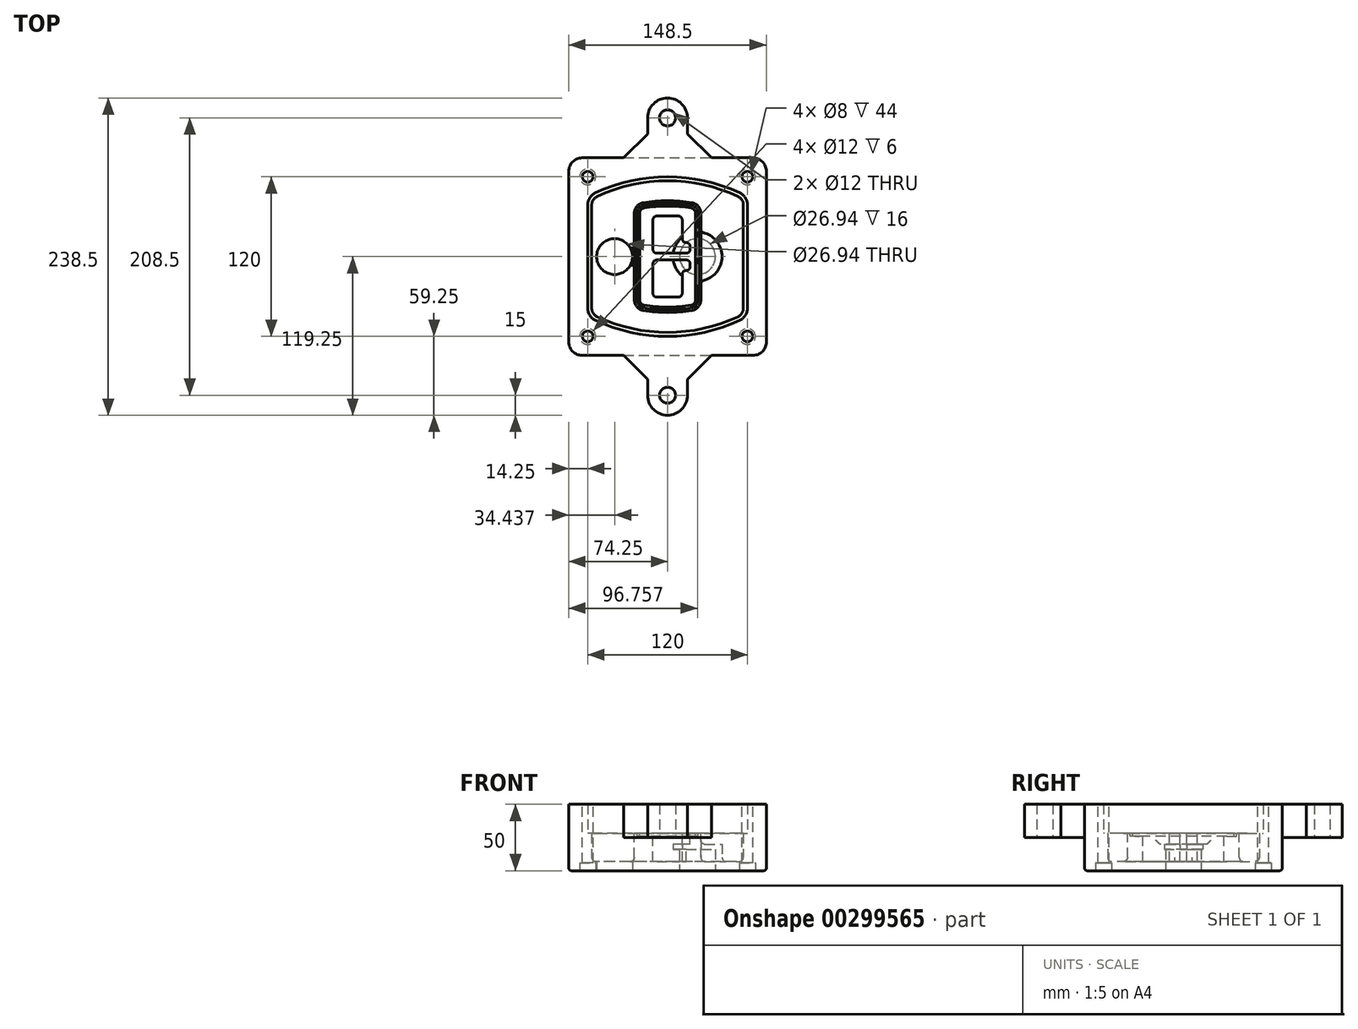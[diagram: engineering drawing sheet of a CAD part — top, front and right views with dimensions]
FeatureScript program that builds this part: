
annotation { "Feature Type Name" : "Feature", "Feature Type Description" : "" }
export const myFeature = defineFeature(function(context is Context, id is Id, definition is map)
    precondition{}
    {
        {
            var Q0;
            Q0=qCreatedBy(makeId("Top.planeOp"),FACE);
            var sketch = newSketch(context, id + "F0", { "sketchPlane" : qUnion([Q0])});
            skPoint(sketch, "E0.rect.middle", {"position": v(0, 0) * mm});
            skLineSegment(sketch, "E1.bottom", {"start": v(-64.25, -74.25) * mm, "end": v(64.25, -74.25) * mm});
            skLineSegment(sketch, "E1.top", {"start": v(-64.25, 74.25) * mm, "end": v(64.25, 74.25) * mm});
            skLineSegment(sketch, "E1.left", {"start": v(-74.25, -64.25) * mm, "end": v(-74.25, 64.25) * mm});
            skLineSegment(sketch, "E1.right", {"start": v(74.25, -64.25) * mm, "end": v(74.25, 64.25) * mm});
            skLineSegment(sketch, "E2", {"start": v(-74.25, 74.25) * mm, "end": v(74.25, -74.25) * mm, "construction": true});
            skLineSegment(sketch, "E3", {"start": v(74.25, 74.25) * mm, "end": v(-74.25, -74.25) * mm, "construction": true});
            skCircle(sketch, "E4", {"center": v(-60, 60) * mm, "radius": 4 * mm});
            skCircle(sketch, "E5", {"center": v(60, 60) * mm, "radius": 4 * mm});
            skCircle(sketch, "E6", {"center": v(60, -60) * mm, "radius": 4 * mm});
            skCircle(sketch, "E7", {"center": v(-60, -60) * mm, "radius": 4 * mm});
            skLineSegment(sketch, "E8", {"start": v(-60, 60) * mm, "end": v(60, 60) * mm, "construction": true});
            skLineSegment(sketch, "E9", {"start": v(60, 60) * mm, "end": v(60, -60) * mm, "construction": true});
            skLineSegment(sketch, "E10", {"start": v(60, -60) * mm, "end": v(-60, -60) * mm, "construction": true});
            skLineSegment(sketch, "E11", {"start": v(-60, -60) * mm, "end": v(-60, 60) * mm, "construction": true});
            skLineSegment(sketch, "E12", {"start": v(-60, 38.83) * mm, "end": v(-60, -38.83) * mm});
            skLineSegment(sketch, "E13", {"start": v(60, 38.83) * mm, "end": v(60, -38.83) * mm});
            skArc(sketch, "E14", {"start": v(54.26, 47.88) * mm, "mid": v(0, 60) * mm, "end": v(-54.26, 47.88) * mm});
            skArc(sketch, "E15", {"start": v(-54.26, -47.88) * mm, "mid": v(0, -60) * mm, "end": v(54.26, -47.88) * mm});
            skLineSegment(sketch, "E16", {"start": v(-60, 0) * mm, "end": v(60, 0) * mm, "construction": true});
            skPoint(sketch, "E17.visualSharp", {"position": v(-60, -45) * mm});
            skArc(sketch, "E17.filletArc", {"start": v(-60, -38.83) * mm, "mid": v(-58.44, -44.2) * mm, "end": v(-54.26, -47.88) * mm});
            skPoint(sketch, "E18.visualSharp", {"position": v(-60, 45) * mm});
            skArc(sketch, "E18.filletArc", {"start": v(-54.26, 47.88) * mm, "mid": v(-58.44, 44.2) * mm, "end": v(-60, 38.83) * mm});
            skPoint(sketch, "E19.visualSharp", {"position": v(60, 45) * mm});
            skArc(sketch, "E19.filletArc", {"start": v(60, 38.83) * mm, "mid": v(58.44, 44.2) * mm, "end": v(54.26, 47.88) * mm});
            skPoint(sketch, "E20.visualSharp", {"position": v(60, -45) * mm});
            skArc(sketch, "E20.filletArc", {"start": v(54.26, -47.88) * mm, "mid": v(58.44, -44.2) * mm, "end": v(60, -38.83) * mm});
            skPoint(sketch, "E21.visualSharp", {"position": v(-74.25, 74.25) * mm});
            skArc(sketch, "E21.filletArc", {"start": v(-64.25, 74.25) * mm, "mid": v(-71.32, 71.32) * mm, "end": v(-74.25, 64.25) * mm});
            skPoint(sketch, "E22.visualSharp", {"position": v(74.25, 74.25) * mm});
            skArc(sketch, "E22.filletArc", {"start": v(74.25, 64.25) * mm, "mid": v(71.32, 71.32) * mm, "end": v(64.25, 74.25) * mm});
            skPoint(sketch, "E23.visualSharp", {"position": v(74.25, -74.25) * mm});
            skArc(sketch, "E23.filletArc", {"start": v(64.25, -74.25) * mm, "mid": v(71.32, -71.32) * mm, "end": v(74.25, -64.25) * mm});
            skPoint(sketch, "E24.visualSharp", {"position": v(-74.25, -74.25) * mm});
            skArc(sketch, "E24.filletArc", {"start": v(-74.25, -64.25) * mm, "mid": v(-71.32, -71.32) * mm, "end": v(-64.25, -74.25) * mm});
            skArc(sketch, "E25.0", {"start": v(57, 38.83) * mm, "mid": v(55.9, 42.58) * mm, "end": v(52.98, 45.17) * mm});
            skLineSegment(sketch, "E25.1", {"start": v(57, 38.83) * mm, "end": v(57, -38.83) * mm});
            skArc(sketch, "E25.2", {"start": v(52.98, -45.17) * mm, "mid": v(55.9, -42.58) * mm, "end": v(57, -38.83) * mm});
            skArc(sketch, "E25.3", {"start": v(-52.98, -45.17) * mm, "mid": v(0, -57) * mm, "end": v(52.98, -45.17) * mm});
            skArc(sketch, "E25.4", {"start": v(-57, -38.83) * mm, "mid": v(-55.9, -42.58) * mm, "end": v(-52.98, -45.17) * mm});
            skArc(sketch, "E25.5", {"start": v(52.98, 45.17) * mm, "mid": v(0, 57) * mm, "end": v(-52.98, 45.17) * mm});
            skLineSegment(sketch, "E25.6", {"start": v(-57, 38.83) * mm, "end": v(-57, -38.83) * mm});
            skArc(sketch, "E25.7", {"start": v(-52.98, 45.17) * mm, "mid": v(-55.9, 42.58) * mm, "end": v(-57, 38.83) * mm});
            skArc(sketch, "E26.0", {"start": v(-55.96, 51.5) * mm, "mid": v(-61.82, 46.33) * mm, "end": v(-64, 38.83) * mm});
            skArc(sketch, "E26.1", {"start": v(55.96, 51.5) * mm, "mid": v(0, 64) * mm, "end": v(-55.96, 51.5) * mm});
            skArc(sketch, "E26.2", {"start": v(64, 38.83) * mm, "mid": v(61.82, 46.33) * mm, "end": v(55.96, 51.5) * mm});
            skLineSegment(sketch, "E26.3", {"start": v(64, 38.83) * mm, "end": v(64, -38.83) * mm});
            skArc(sketch, "E26.4", {"start": v(55.96, -51.5) * mm, "mid": v(61.82, -46.33) * mm, "end": v(64, -38.83) * mm});
            skLineSegment(sketch, "E26.5", {"start": v(-64, 38.83) * mm, "end": v(-64, -38.83) * mm});
            skArc(sketch, "E26.6", {"start": v(-55.96, -51.5) * mm, "mid": v(0, -64) * mm, "end": v(55.96, -51.5) * mm});
            skArc(sketch, "E26.7", {"start": v(-64, -38.83) * mm, "mid": v(-61.82, -46.33) * mm, "end": v(-55.96, -51.5) * mm});
            skSolve(sketch);
        }
        {
            var Q0;
            Q0=makeQuery(id+"F0.imprint","IMPRINT",FACE,{"disambiguationData":[TD([[makeQuery(id+"F0.imprint","IMPRINT",EDGE,{"derivedFrom":sQuery(id+"F0.wireOp",EDGE,"E1.bottom")}),1.0]])]});
            var Q1;
            Q1=makeQuery(id+"F0.imprint","IMPRINT",FACE,{"disambiguationData":[TD([[makeQuery(id+"F0.imprint","IMPRINT",EDGE,{"derivedFrom":sQuery(id+"F0.wireOp",EDGE,"E12")}),1.0]])]});
            var Q2;
            Q2=makeQuery(id+"F0.imprint","IMPRINT",FACE,{"disambiguationData":[TD([[makeQuery(id+"F0.imprint","IMPRINT",EDGE,{"derivedFrom":sQuery(id+"F0.wireOp",EDGE,"E25.0")}),1.0]])]});
            var Q3;
            Q3=makeQuery(id+"F0.imprint","IMPRINT",FACE,{"disambiguationData":[TD([[makeQuery(id+"F0.imprint","IMPRINT",EDGE,{"derivedFrom":sQuery(id+"F0.wireOp",EDGE,"E12")}),-1.0]])]});
            extrude(context, id + "F1", {"entities" : qUnion([Q0, Q1, Q2, Q3]), "oppositeDirection" : true, "depth" : 25 * mm});
        }
        {
            var Q0;
            Q0=makeQuery(id+"F0.imprint","IMPRINT",FACE,{"disambiguationData":[TD([[makeQuery(id+"F0.imprint","IMPRINT",EDGE,{"derivedFrom":sQuery(id+"F0.wireOp",EDGE,"E12")}),1.0]])]});
            extrude(context, id + "F2", {"entities" : qUnion([Q0]), "operationType" : NewBodyOperationType.ADD, "depth" : 3 * mm});
        }
        {
            var Q0;
            Q0=makeQuery(id+"F0.imprint","IMPRINT",FACE,{"disambiguationData":[TD([[makeQuery(id+"F0.imprint","IMPRINT",EDGE,{"derivedFrom":sQuery(id+"F0.wireOp",EDGE,"E25.0")}),1.0]])]});
            extrude(context, id + "F3", {"entities" : qUnion([Q0]), "operationType" : NewBodyOperationType.REMOVE, "oppositeDirection" : true, "depth" : 18 * mm});
        }
        {
            var Q0;
            Q0=makeQuery(id+"F2.opExtrude","CAP_FACE",FACE,{"disambiguationData":[OSD([sQuery(id+"F0.wireOp",EDGE,"E12"),sQuery(id+"F0.wireOp",EDGE,"E13"),sQuery(id+"F0.wireOp",EDGE,"E14"),sQuery(id+"F0.wireOp",EDGE,"E15"),sQuery(id+"F0.wireOp",EDGE,"E17.filletArc"),sQuery(id+"F0.wireOp",EDGE,"E18.filletArc"),sQuery(id+"F0.wireOp",EDGE,"E19.filletArc"),sQuery(id+"F0.wireOp",EDGE,"E20.filletArc"),sQuery(id+"F0.wireOp",EDGE,"E25.0"),sQuery(id+"F0.wireOp",EDGE,"E25.1"),sQuery(id+"F0.wireOp",EDGE,"E25.2"),sQuery(id+"F0.wireOp",EDGE,"E25.3"),sQuery(id+"F0.wireOp",EDGE,"E25.4"),sQuery(id+"F0.wireOp",EDGE,"E25.5"),sQuery(id+"F0.wireOp",EDGE,"E25.6"),sQuery(id+"F0.wireOp",EDGE,"E25.7")])],"isStart":false});
            var sketch = newSketch(context, id + "F4", { "sketchPlane" : qUnion([Q0])});
            skArc(sketch, "E27.0", {"start": v(-18.34, -40.45) * mm, "mid": v(0, -42) * mm, "end": v(18.34, -40.45) * mm});
            skArc(sketch, "E28.0", {"start": v(18.34, 40.45) * mm, "mid": v(0, 42) * mm, "end": v(-18.34, 40.45) * mm});
            skLineSegment(sketch, "E29", {"start": v(-25, 32.57) * mm, "end": v(-25, -32.57) * mm});
            skLineSegment(sketch, "E30", {"start": v(25, 32.57) * mm, "end": v(25, -32.57) * mm});
            skLineSegment(sketch, "E31", {"start": v(-25, 39.1) * mm, "end": v(25, 39.1) * mm, "construction": true});
            skLineSegment(sketch, "E32", {"start": v(-25, -39.1) * mm, "end": v(25, -39.1) * mm, "construction": true});
            skPoint(sketch, "E33.visualSharp", {"position": v(-25, 39.1) * mm});
            skArc(sketch, "E33.filletArc", {"start": v(-18.34, 40.45) * mm, "mid": v(-23.11, 37.73) * mm, "end": v(-25, 32.57) * mm});
            skPoint(sketch, "E34.visualSharp", {"position": v(25, 39.1) * mm});
            skArc(sketch, "E34.filletArc", {"start": v(25, 32.57) * mm, "mid": v(23.11, 37.73) * mm, "end": v(18.34, 40.45) * mm});
            skPoint(sketch, "E35.visualSharp", {"position": v(25, -39.1) * mm});
            skArc(sketch, "E35.filletArc", {"start": v(18.34, -40.45) * mm, "mid": v(23.11, -37.73) * mm, "end": v(25, -32.57) * mm});
            skPoint(sketch, "E36.visualSharp", {"position": v(-25, -39.1) * mm});
            skArc(sketch, "E36.filletArc", {"start": v(-25, -32.57) * mm, "mid": v(-23.11, -37.73) * mm, "end": v(-18.34, -40.45) * mm});
            skArc(sketch, "E37.0", {"start": v(52.98, 45.17) * mm, "mid": v(0, 57) * mm, "end": v(-52.98, 45.17) * mm});
            skArc(sketch, "E37.1", {"start": v(-52.98, 45.17) * mm, "mid": v(-55.9, 42.58) * mm, "end": v(-57, 38.83) * mm});
            skLineSegment(sketch, "E37.2", {"start": v(-57, 38.83) * mm, "end": v(-57, -38.83) * mm});
            skArc(sketch, "E37.3", {"start": v(-57, -38.83) * mm, "mid": v(-55.9, -42.58) * mm, "end": v(-52.98, -45.17) * mm});
            skArc(sketch, "E37.4", {"start": v(-52.98, -45.17) * mm, "mid": v(0, -57) * mm, "end": v(52.98, -45.17) * mm});
            skArc(sketch, "E37.5", {"start": v(52.98, -45.17) * mm, "mid": v(55.9, -42.58) * mm, "end": v(57, -38.83) * mm});
            skLineSegment(sketch, "E37.6", {"start": v(57, 38.83) * mm, "end": v(57, -38.83) * mm});
            skArc(sketch, "E37.7", {"start": v(57, 38.83) * mm, "mid": v(55.9, 42.58) * mm, "end": v(52.98, 45.17) * mm});
            skLineSegment(sketch, "E38.0", {"start": v(23, 32.57) * mm, "end": v(23, -32.57) * mm});
            skArc(sketch, "E38.1", {"start": v(18, -38.48) * mm, "mid": v(21.58, -36.44) * mm, "end": v(23, -32.57) * mm});
            skArc(sketch, "E38.2", {"start": v(-18, -38.48) * mm, "mid": v(0, -40) * mm, "end": v(18, -38.48) * mm});
            skArc(sketch, "E38.3", {"start": v(-23, -32.57) * mm, "mid": v(-21.58, -36.44) * mm, "end": v(-18, -38.48) * mm});
            skLineSegment(sketch, "E38.4", {"start": v(-23, 32.57) * mm, "end": v(-23, -32.57) * mm});
            skArc(sketch, "E38.5", {"start": v(23, 32.57) * mm, "mid": v(21.58, 36.44) * mm, "end": v(18, 38.48) * mm});
            skArc(sketch, "E38.6", {"start": v(-18, 38.48) * mm, "mid": v(-21.58, 36.44) * mm, "end": v(-23, 32.57) * mm});
            skArc(sketch, "E38.7", {"start": v(18, 38.48) * mm, "mid": v(0, 40) * mm, "end": v(-18, 38.48) * mm});
            skArc(sketch, "E39.0", {"start": v(21, 32.57) * mm, "mid": v(20.06, 35.15) * mm, "end": v(17.67, 36.5) * mm});
            skLineSegment(sketch, "E39.1", {"start": v(21, 32.57) * mm, "end": v(21, -32.57) * mm});
            skArc(sketch, "E39.2", {"start": v(17.67, -36.5) * mm, "mid": v(20.06, -35.15) * mm, "end": v(21, -32.57) * mm});
            skArc(sketch, "E39.3", {"start": v(-17.67, -36.5) * mm, "mid": v(0, -38) * mm, "end": v(17.67, -36.5) * mm});
            skArc(sketch, "E39.4", {"start": v(-21, -32.57) * mm, "mid": v(-20.06, -35.15) * mm, "end": v(-17.67, -36.5) * mm});
            skArc(sketch, "E39.5", {"start": v(17.67, 36.5) * mm, "mid": v(0, 38) * mm, "end": v(-17.67, 36.5) * mm});
            skLineSegment(sketch, "E39.6", {"start": v(-21, 32.57) * mm, "end": v(-21, -32.57) * mm});
            skArc(sketch, "E39.7", {"start": v(-17.67, 36.5) * mm, "mid": v(-20.06, 35.15) * mm, "end": v(-21, 32.57) * mm});
            skLineSegment(sketch, "E40", {"start": v(-25, 0) * mm, "end": v(25, 0) * mm, "construction": true});
            skLineSegment(sketch, "E41", {"start": v(-11, 5.5) * mm, "end": v(-11, 27.5) * mm});
            skLineSegment(sketch, "E42", {"start": v(-8, 30.5) * mm, "end": v(8, 30.5) * mm});
            skLineSegment(sketch, "E43", {"start": v(11, 27.5) * mm, "end": v(11, 13.5) * mm});
            skLineSegment(sketch, "E44", {"start": v(14, 10.5) * mm, "end": v(14, 10.5) * mm});
            skLineSegment(sketch, "E45", {"start": v(17, 7.5) * mm, "end": v(17, 5.5) * mm});
            skLineSegment(sketch, "E46", {"start": v(14, 2.5) * mm, "end": v(-8, 2.5) * mm});
            skPoint(sketch, "E47.visualSharp", {"position": v(-11, 30.5) * mm});
            skArc(sketch, "E47.filletArc", {"start": v(-8, 30.5) * mm, "mid": v(-10.12, 29.62) * mm, "end": v(-11, 27.5) * mm});
            skPoint(sketch, "E48.visualSharp", {"position": v(11, 30.5) * mm});
            skArc(sketch, "E48.filletArc", {"start": v(11, 27.5) * mm, "mid": v(10.12, 29.62) * mm, "end": v(8, 30.5) * mm});
            skPoint(sketch, "E49.visualSharp", {"position": v(11, 10.5) * mm});
            skArc(sketch, "E49.filletArc", {"start": v(11, 13.5) * mm, "mid": v(11.88, 11.38) * mm, "end": v(14, 10.5) * mm});
            skPoint(sketch, "E50.visualSharp", {"position": v(17, 10.5) * mm});
            skArc(sketch, "E50.filletArc", {"start": v(17, 7.5) * mm, "mid": v(16.12, 9.62) * mm, "end": v(14, 10.5) * mm});
            skPoint(sketch, "E51.visualSharp", {"position": v(17, 2.5) * mm});
            skArc(sketch, "E51.filletArc", {"start": v(14, 2.5) * mm, "mid": v(16.12, 3.38) * mm, "end": v(17, 5.5) * mm});
            skPoint(sketch, "E52.visualSharp", {"position": v(-11, 2.5) * mm});
            skArc(sketch, "E52.filletArc", {"start": v(-11, 5.5) * mm, "mid": v(-10.12, 3.38) * mm, "end": v(-8, 2.5) * mm});
            skLineSegment(sketch, "E53.0.MirrorCS", {"start": v(14, -2.5) * mm, "end": v(-8, -2.5) * mm});
            skArc(sketch, "E54.0.MirrorCS", {"start": v(-11, -5.5) * mm, "mid": v(-10.12, -3.38) * mm, "end": v(-8, -2.5) * mm});
            skLineSegment(sketch, "E55.0.MirrorCS", {"start": v(-11, -5.5) * mm, "end": v(-11, -27.5) * mm});
            skArc(sketch, "E56.0.MirrorCS", {"start": v(-8, -30.5) * mm, "mid": v(-10.12, -29.62) * mm, "end": v(-11, -27.5) * mm});
            skLineSegment(sketch, "E57.0.MirrorCS", {"start": v(-8, -30.5) * mm, "end": v(8, -30.5) * mm});
            skArc(sketch, "E58.0.MirrorCS", {"start": v(11, -27.5) * mm, "mid": v(10.12, -29.62) * mm, "end": v(8, -30.5) * mm});
            skLineSegment(sketch, "E59.0.MirrorCS", {"start": v(11, -27.5) * mm, "end": v(11, -13.5) * mm});
            skArc(sketch, "E60.0.MirrorCS", {"start": v(11, -13.5) * mm, "mid": v(11.88, -11.38) * mm, "end": v(14, -10.5) * mm});
            skArc(sketch, "E61.0.MirrorCS", {"start": v(17, -7.5) * mm, "mid": v(16.12, -9.62) * mm, "end": v(14, -10.5) * mm});
            skLineSegment(sketch, "E62.0.MirrorCS", {"start": v(17, -7.5) * mm, "end": v(17, -5.5) * mm});
            skArc(sketch, "E63.0.MirrorCS", {"start": v(14, -2.5) * mm, "mid": v(16.12, -3.38) * mm, "end": v(17, -5.5) * mm});
            skSolve(sketch);
        }
        {
            var Q0;
            Q0=makeQuery(id+"F4.imprint","IMPRINT",FACE,{"disambiguationData":[TD([[makeQuery(id+"F4.imprint","IMPRINT",EDGE,{"derivedFrom":sQuery(id+"F4.wireOp",EDGE,"E27.0")}),1.0]])]});
            var Q1;
            Q1=makeQuery(id+"F4.imprint","IMPRINT",FACE,{"disambiguationData":[TD([[makeQuery(id+"F4.imprint","IMPRINT",EDGE,{"derivedFrom":sQuery(id+"F4.wireOp",EDGE,"E38.0")}),-1.0]])]});
            var Q2;
            Q2=makeQuery(id+"F4.imprint","IMPRINT",FACE,{"disambiguationData":[TD([[makeQuery(id+"F4.imprint","IMPRINT",EDGE,{"derivedFrom":sQuery(id+"F4.wireOp",EDGE,"E39.0")}),1.0]])]});
            extrude(context, id + "F5", {"entities" : qUnion([Q0, Q1, Q2]), "operationType" : NewBodyOperationType.ADD, "endBound" : BoundingType.UP_TO_NEXT, "oppositeDirection" : true, "depth" : 25 * mm});
        }
        {
            var Q0;
            Q0=makeQuery(id+"F4.imprint","IMPRINT",FACE,{"disambiguationData":[TD([[makeQuery(id+"F4.imprint","IMPRINT",EDGE,{"derivedFrom":sQuery(id+"F4.wireOp",EDGE,"E38.0")}),-1.0]])]});
            extrude(context, id + "F6", {"entities" : qUnion([Q0]), "operationType" : NewBodyOperationType.REMOVE, "oppositeDirection" : true, "depth" : 2 * mm});
        }
        {
            var Q0;
            Q0=makeQuery(id+"F1.opExtrude","CAP_FACE",FACE,{"disambiguationData":[OSD([sQuery(id+"F0.wireOp",EDGE,"E1.bottom"),sQuery(id+"F0.wireOp",EDGE,"E1.top"),sQuery(id+"F0.wireOp",EDGE,"E1.left"),sQuery(id+"F0.wireOp",EDGE,"E1.right"),sQuery(id+"F0.wireOp",EDGE,"E4"),sQuery(id+"F0.wireOp",EDGE,"E5"),sQuery(id+"F0.wireOp",EDGE,"E6"),sQuery(id+"F0.wireOp",EDGE,"E7"),sQuery(id+"F0.wireOp",EDGE,"E21.filletArc"),sQuery(id+"F0.wireOp",EDGE,"E22.filletArc"),sQuery(id+"F0.wireOp",EDGE,"E23.filletArc"),sQuery(id+"F0.wireOp",EDGE,"E24.filletArc")])],"isStart":false});
            var sketch = newSketch(context, id + "F7", { "sketchPlane" : qUnion([Q0])});
            skCircle(sketch, "E64", {"center": v(22.5, 0) * mm, "radius": 13.47 * mm});
            skCircle(sketch, "E65", {"center": v(-39.81, 0) * mm, "radius": 13.47 * mm});
            skLineSegment(sketch, "E66", {"start": v(74.25, 0) * mm, "end": v(-74.25, 0) * mm});
            skCircle(sketch, "E67", {"center": v(22.5, 0) * mm, "radius": 18.47 * mm});
            skCircle(sketch, "E68", {"center": v(60, -60) * mm, "radius": 6 * mm});
            skCircle(sketch, "E69", {"center": v(-60, -60) * mm, "radius": 6 * mm});
            skCircle(sketch, "E70", {"center": v(-60, 60) * mm, "radius": 6 * mm});
            skCircle(sketch, "E71", {"center": v(60, 60) * mm, "radius": 6 * mm});
            skSolve(sketch);
        }
        {
            var Q0;
            {var subQ1=sQuery(id+"F7.wireOp",EDGE,"E66");var subQ4=sQuery(id+"F7.wireOp",EDGE,"E64");var subQ6=makeQuery(id+"F7.imprint","INTERSECT",VERTEX,{"disambiguationData":[OD(0.0)],"derivedFrom":[subQ4,subQ1]});Q0=makeQuery(id+"F7.imprint","IMPRINT",FACE,{"disambiguationData":[TD([[makeQuery(id+"F7.imprint","IMPRINT",EDGE,{"disambiguationData":[TD([[subQ6,-1.0]])],"derivedFrom":subQ4}),-1.0]])]});}
            var Q1;
            {var subQ0=sQuery(id+"F7.wireOp",EDGE,"E66");var subQ1=sQuery(id+"F7.wireOp",EDGE,"E64");var subQ3=makeQuery(id+"F7.imprint","INTERSECT",VERTEX,{"disambiguationData":[OD(0.0)],"derivedFrom":[subQ1,subQ0]});Q1=makeQuery(id+"F7.imprint","IMPRINT",FACE,{"disambiguationData":[TD([[makeQuery(id+"F7.imprint","IMPRINT",EDGE,{"disambiguationData":[TD([[subQ3,-1.0]])],"derivedFrom":subQ1}),1.0]])]});}
            var Q2;
            {var subQ0=sQuery(id+"F7.wireOp",EDGE,"E66");var subQ1=sQuery(id+"F7.wireOp",EDGE,"E64");var subQ3=makeQuery(id+"F7.imprint","INTERSECT",VERTEX,{"disambiguationData":[OD(0.0)],"derivedFrom":[subQ1,subQ0]});Q2=makeQuery(id+"F7.imprint","IMPRINT",FACE,{"disambiguationData":[TD([[makeQuery(id+"F7.imprint","IMPRINT",EDGE,{"disambiguationData":[TD([[subQ3,1.0]])],"derivedFrom":subQ1}),1.0]])]});}
            var Q3;
            {var subQ1=sQuery(id+"F7.wireOp",EDGE,"E66");var subQ4=sQuery(id+"F7.wireOp",EDGE,"E64");var subQ6=makeQuery(id+"F7.imprint","INTERSECT",VERTEX,{"disambiguationData":[OD(0.0)],"derivedFrom":[subQ4,subQ1]});Q3=makeQuery(id+"F7.imprint","IMPRINT",FACE,{"disambiguationData":[TD([[makeQuery(id+"F7.imprint","IMPRINT",EDGE,{"disambiguationData":[TD([[subQ6,1.0]])],"derivedFrom":subQ4}),-1.0]])]});}
            extrude(context, id + "F8", {"entities" : qUnion([Q0, Q1, Q2, Q3]), "operationType" : NewBodyOperationType.ADD, "oppositeDirection" : true, "depth" : 20 * mm});
        }
        {
            var Q0;
            {var subQ0=sQuery(id+"F7.wireOp",EDGE,"E66");var subQ1=sQuery(id+"F7.wireOp",EDGE,"E64");var subQ3=makeQuery(id+"F7.imprint","INTERSECT",VERTEX,{"disambiguationData":[OD(0.0)],"derivedFrom":[subQ1,subQ0]});Q0=makeQuery(id+"F7.imprint","IMPRINT",FACE,{"disambiguationData":[TD([[makeQuery(id+"F7.imprint","IMPRINT",EDGE,{"disambiguationData":[TD([[subQ3,-1.0]])],"derivedFrom":subQ1}),1.0]])]});}
            var Q1;
            {var subQ0=sQuery(id+"F7.wireOp",EDGE,"E66");var subQ1=sQuery(id+"F7.wireOp",EDGE,"E64");var subQ3=makeQuery(id+"F7.imprint","INTERSECT",VERTEX,{"disambiguationData":[OD(0.0)],"derivedFrom":[subQ1,subQ0]});Q1=makeQuery(id+"F7.imprint","IMPRINT",FACE,{"disambiguationData":[TD([[makeQuery(id+"F7.imprint","IMPRINT",EDGE,{"disambiguationData":[TD([[subQ3,1.0]])],"derivedFrom":subQ1}),1.0]])]});}
            extrude(context, id + "F9", {"entities" : qUnion([Q0, Q1]), "operationType" : NewBodyOperationType.REMOVE, "oppositeDirection" : true, "depth" : 16 * mm});
        }
        {
            var Q0;
            {var subQ0=sQuery(id+"F7.wireOp",EDGE,"E66");var subQ1=sQuery(id+"F7.wireOp",EDGE,"E65");var subQ3=makeQuery(id+"F7.imprint","INTERSECT",VERTEX,{"disambiguationData":[OD(0.0)],"derivedFrom":[subQ1,subQ0]});Q0=makeQuery(id+"F7.imprint","IMPRINT",FACE,{"disambiguationData":[TD([[makeQuery(id+"F7.imprint","IMPRINT",EDGE,{"disambiguationData":[TD([[subQ3,-1.0]])],"derivedFrom":subQ1}),1.0]])]});}
            var Q1;
            {var subQ0=sQuery(id+"F7.wireOp",EDGE,"E66");var subQ1=sQuery(id+"F7.wireOp",EDGE,"E65");var subQ3=makeQuery(id+"F7.imprint","INTERSECT",VERTEX,{"disambiguationData":[OD(0.0)],"derivedFrom":[subQ1,subQ0]});Q1=makeQuery(id+"F7.imprint","IMPRINT",FACE,{"disambiguationData":[TD([[makeQuery(id+"F7.imprint","IMPRINT",EDGE,{"disambiguationData":[TD([[subQ3,1.0]])],"derivedFrom":subQ1}),1.0]])]});}
            extrude(context, id + "F10", {"entities" : qUnion([Q0, Q1]), "operationType" : NewBodyOperationType.REMOVE, "oppositeDirection" : true, "depth" : 25 * mm});
        }
        {
            var Q0;
            Q0=makeQuery(id+"F7.imprint","IMPRINT",FACE,{"disambiguationData":[TD([[makeQuery(id+"F7.imprint","IMPRINT",EDGE,{"derivedFrom":sQuery(id+"F7.wireOp",EDGE,"E68")}),1.0]])]});
            var Q1;
            Q1=makeQuery(id+"F7.imprint","IMPRINT",FACE,{"disambiguationData":[TD([[makeQuery(id+"F7.imprint","IMPRINT",EDGE,{"derivedFrom":makeQuery(id+"F1.opExtrude","CAP_EDGE",EDGE,{"disambiguationData":[OSD([sQuery(id+"F0.wireOp",EDGE,"E5")])],"isStart":false})}),-1.0]])]});
            var Q2;
            Q2=makeQuery(id+"F7.imprint","IMPRINT",FACE,{"disambiguationData":[TD([[makeQuery(id+"F7.imprint","IMPRINT",EDGE,{"derivedFrom":sQuery(id+"F7.wireOp",EDGE,"E69")}),1.0]])]});
            var Q3;
            Q3=makeQuery(id+"F7.imprint","IMPRINT",FACE,{"disambiguationData":[TD([[makeQuery(id+"F7.imprint","IMPRINT",EDGE,{"derivedFrom":makeQuery(id+"F1.opExtrude","CAP_EDGE",EDGE,{"disambiguationData":[OSD([sQuery(id+"F0.wireOp",EDGE,"E4")])],"isStart":false})}),-1.0]])]});
            var Q4;
            Q4=makeQuery(id+"F7.imprint","IMPRINT",FACE,{"disambiguationData":[TD([[makeQuery(id+"F7.imprint","IMPRINT",EDGE,{"derivedFrom":sQuery(id+"F7.wireOp",EDGE,"E70")}),1.0]])]});
            var Q5;
            Q5=makeQuery(id+"F7.imprint","IMPRINT",FACE,{"disambiguationData":[TD([[makeQuery(id+"F7.imprint","IMPRINT",EDGE,{"derivedFrom":makeQuery(id+"F1.opExtrude","CAP_EDGE",EDGE,{"disambiguationData":[OSD([sQuery(id+"F0.wireOp",EDGE,"E7")])],"isStart":false})}),-1.0]])]});
            var Q6;
            Q6=makeQuery(id+"F7.imprint","IMPRINT",FACE,{"disambiguationData":[TD([[makeQuery(id+"F7.imprint","IMPRINT",EDGE,{"derivedFrom":sQuery(id+"F7.wireOp",EDGE,"E71")}),1.0]])]});
            var Q7;
            Q7=makeQuery(id+"F7.imprint","IMPRINT",FACE,{"disambiguationData":[TD([[makeQuery(id+"F7.imprint","IMPRINT",EDGE,{"derivedFrom":makeQuery(id+"F1.opExtrude","CAP_EDGE",EDGE,{"disambiguationData":[OSD([sQuery(id+"F0.wireOp",EDGE,"E6")])],"isStart":false})}),-1.0]])]});
            extrude(context, id + "F11", {"entities" : qUnion([Q0, Q1, Q2, Q3, Q4, Q5, Q6, Q7]), "operationType" : NewBodyOperationType.REMOVE, "oppositeDirection" : true, "depth" : 6 * mm});
        }
        {
            var Q0;
            Q0=makeQuery(id+"F9.boolean.opBoolean","COPY",FACE,{"derivedFrom":makeQuery(id+"F9.opExtrude","CAP_FACE",FACE,{"disambiguationData":[OSD([sQuery(id+"F7.wireOp",EDGE,"E64")])],"isStart":false})});
            var sketch = newSketch(context, id + "F12", { "sketchPlane" : qUnion([Q0])});
            skArc(sketch, "E72.0", {"start": v(11, 14.45) * mm, "mid": v(6.45, 9.13) * mm, "end": v(4.2, 2.5) * mm});
            skArc(sketch, "E72.1", {"start": v(4.2, -2.5) * mm, "mid": v(6.45, -9.13) * mm, "end": v(11, -14.45) * mm});
            skLineSegment(sketch, "E73", {"start": v(4.2, -2.5) * mm, "end": v(14, -2.5) * mm});
            skLineSegment(sketch, "E74.0", {"start": v(14, 2.5) * mm, "end": v(4.2, 2.5) * mm});
            skArc(sketch, "E74.1", {"start": v(14, 2.5) * mm, "mid": v(16.12, 3.38) * mm, "end": v(17, 5.5) * mm});
            skLineSegment(sketch, "E74.2", {"start": v(17, 7.5) * mm, "end": v(17, 5.5) * mm});
            skArc(sketch, "E74.3", {"start": v(17, 7.5) * mm, "mid": v(16.12, 9.62) * mm, "end": v(14, 10.5) * mm});
            skArc(sketch, "E74.4", {"start": v(11, 13.5) * mm, "mid": v(11.88, 11.38) * mm, "end": v(14, 10.5) * mm});
            skLineSegment(sketch, "E74.5", {"start": v(11, 14.45) * mm, "end": v(11, 13.5) * mm});
            skLineSegment(sketch, "E74.7", {"start": v(14, -2.5) * mm, "end": v(4.2, -2.5) * mm});
            skArc(sketch, "E74.8", {"start": v(14, -2.5) * mm, "mid": v(16.12, -3.38) * mm, "end": v(17, -5.5) * mm});
            skLineSegment(sketch, "E74.9", {"start": v(17, -7.5) * mm, "end": v(17, -5.5) * mm});
            skArc(sketch, "E74.10", {"start": v(17, -7.5) * mm, "mid": v(16.12, -9.62) * mm, "end": v(14, -10.5) * mm});
            skArc(sketch, "E74.11", {"start": v(11, -13.5) * mm, "mid": v(11.88, -11.38) * mm, "end": v(14, -10.5) * mm});
            skLineSegment(sketch, "E74.12", {"start": v(11, -14.45) * mm, "end": v(11, -13.5) * mm});
            skPoint(sketch, "E75.orphan", {"position": v(11, -27.5) * mm});
            skPoint(sketch, "E76.orphan", {"position": v(-8, -2.5) * mm});
            skPoint(sketch, "E77.orphan", {"position": v(-8, 2.5) * mm});
            skPoint(sketch, "E78.orphan", {"position": v(11, 27.5) * mm});
            skSolve(sketch);
        }
        {
            var Q0;
            {var subQ7=sQuery(id+"F12.wireOp",EDGE,"E72.0");var subQ14=sQuery(id+"F12.wireOp",EDGE,"E72.1");var subQ16=sQuery(id+"F12.wireOp",EDGE,"E74.1");var subQ18=sQuery(id+"F12.wireOp",EDGE,"E74.8");Q0=qUnion([makeQuery(id+"F12.imprint","IMPRINT",FACE,{"disambiguationData":[TD([[makeQuery(id+"F12.imprint","IMPRINT",EDGE,{"derivedFrom":subQ7}),1.0]])]}),makeQuery(id+"F12.imprint","IMPRINT",FACE,{"disambiguationData":[TD([[makeQuery(id+"F12.imprint","IMPRINT",EDGE,{"derivedFrom":subQ14}),1.0]])]}),makeQuery(id+"F12.imprint","IMPRINT",FACE,{"disambiguationData":[TD([[makeQuery(id+"F12.imprint","IMPRINT",EDGE,{"derivedFrom":subQ16}),1.0]])]}),makeQuery(id+"F12.imprint","IMPRINT",FACE,{"disambiguationData":[TD([[makeQuery(id+"F12.imprint","IMPRINT",EDGE,{"derivedFrom":subQ18}),-1.0]])]})]);}
            var Q1;
            Q1=makeQuery(id+"F5.boolean.opBoolean","SPLIT",FACE,{"disambiguationData":[TD([makeQuery(id+"F5.opExtrude","SWEPT_FACE",FACE,{"disambiguationData":[OSD([sQuery(id+"F4.wireOp",EDGE,"E41")])]})])],"derivedFrom":makeQuery(id+"F3.boolean.opBoolean","COPY",FACE,{"derivedFrom":makeQuery(id+"F3.opExtrude","CAP_FACE",FACE,{"disambiguationData":[OSD([sQuery(id+"F0.wireOp",EDGE,"E25.0"),sQuery(id+"F0.wireOp",EDGE,"E25.1"),sQuery(id+"F0.wireOp",EDGE,"E25.2"),sQuery(id+"F0.wireOp",EDGE,"E25.3"),sQuery(id+"F0.wireOp",EDGE,"E25.4"),sQuery(id+"F0.wireOp",EDGE,"E25.5"),sQuery(id+"F0.wireOp",EDGE,"E25.6"),sQuery(id+"F0.wireOp",EDGE,"E25.7")])],"isStart":false})})});
            extrude(context, id + "F13", {"entities" : qUnion([Q0]), "operationType" : NewBodyOperationType.REMOVE, "endBound" : BoundingType.UP_TO_SURFACE, "endBoundEntityFace" : qUnion([Q1]), "depth" : 25 * mm});
        }
        {
            var Q0;
            Q0=makeQuery(id+"F3.boolean.opBoolean","COPY",EDGE,{"derivedFrom":makeQuery(id+"F3.opExtrude","CAP_EDGE",EDGE,{"disambiguationData":[OSD([sQuery(id+"F0.wireOp",EDGE,"E25.6")])],"isStart":false})});
            var Q1;
            Q1=makeQuery(id+"F8.boolean.opBoolean","INTERSECT",EDGE,{"derivedFrom":[makeQuery(id+"F5.opExtrude","SWEPT_FACE",FACE,{"disambiguationData":[OSD([sQuery(id+"F4.wireOp",EDGE,"E30")])]}),makeQuery(id+"F8.opExtrude","CAP_FACE",FACE,{"disambiguationData":[OSD([sQuery(id+"F7.wireOp",EDGE,"E67")])],"isStart":false})]});
            var Q2;
            Q2=makeQuery(id+"F8.boolean.opBoolean","INTERSECT",EDGE,{"disambiguationData":[OD(1.0)],"derivedFrom":[makeQuery(id+"F5.opExtrude","SWEPT_FACE",FACE,{"disambiguationData":[OSD([sQuery(id+"F4.wireOp",EDGE,"E30")])]}),makeQuery(id+"F8.opExtrude","SWEPT_FACE",FACE,{"disambiguationData":[OSD([sQuery(id+"F7.wireOp",EDGE,"E67")])]})]});
            var Q3;
            {var subQ0=sQuery(id+"F4.wireOp",EDGE,"E30");Q3=makeQuery(id+"F8.boolean.opBoolean","SPLIT",EDGE,{"disambiguationData":[TD([makeQuery(id+"F5.opExtrude","SWEPT_FACE",FACE,{"disambiguationData":[OSD([sQuery(id+"F4.wireOp",EDGE,"E35.filletArc")])]})])],"derivedFrom":makeQuery(id+"F5.opExtrude","CAP_EDGE",EDGE,{"disambiguationData":[OSD([subQ0])],"isStart":false})});}
            var Q4;
            {var subQ0=sQuery(id+"F0.wireOp",EDGE,"E25.7");var subQ1=sQuery(id+"F0.wireOp",EDGE,"E25.1");var subQ2=sQuery(id+"F0.wireOp",EDGE,"E25.6");var subQ3=sQuery(id+"F0.wireOp",EDGE,"E25.5");var subQ4=sQuery(id+"F0.wireOp",EDGE,"E25.4");var subQ5=sQuery(id+"F0.wireOp",EDGE,"E25.0");var subQ6=sQuery(id+"F0.wireOp",EDGE,"E25.2");var subQ7=sQuery(id+"F0.wireOp",EDGE,"E25.3");Q4=makeQuery(id+"F8.boolean.opBoolean","INTERSECT",EDGE,{"derivedFrom":[makeQuery(id+"F5.boolean.opBoolean","SPLIT",FACE,{"disambiguationData":[TD([makeQuery(id+"F2.opExtrude","SWEPT_FACE",FACE,{"disambiguationData":[OSD([subQ5])]})])],"derivedFrom":makeQuery(id+"F3.boolean.opBoolean","COPY",FACE,{"derivedFrom":makeQuery(id+"F3.opExtrude","CAP_FACE",FACE,{"disambiguationData":[OSD([subQ5,subQ1,subQ6,subQ7,subQ4,subQ3,subQ2,subQ0])],"isStart":false})})}),makeQuery(id+"F8.opExtrude","SWEPT_FACE",FACE,{"disambiguationData":[OSD([sQuery(id+"F7.wireOp",EDGE,"E67")])]})]});}
            var Q5;
            Q5=makeQuery(id+"F8.boolean.opBoolean","INTERSECT",EDGE,{"disambiguationData":[OD(0.0)],"derivedFrom":[makeQuery(id+"F5.opExtrude","SWEPT_FACE",FACE,{"disambiguationData":[OSD([sQuery(id+"F4.wireOp",EDGE,"E30")])]}),makeQuery(id+"F8.opExtrude","SWEPT_FACE",FACE,{"disambiguationData":[OSD([sQuery(id+"F7.wireOp",EDGE,"E67")])]})]});
            fillet(context, id + "F14", {"entities" : qUnion([Q0, Q1, Q2, Q3, Q4, Q5]), "radius" : 3 * mm, "tangentPropagation" : true, "allowEdgeOverflow" : false});
        }
        {
            var Q0;
            Q0=makeQuery(id+"F1.opExtrude","CAP_EDGE",EDGE,{"disambiguationData":[OSD([sQuery(id+"F0.wireOp",EDGE,"E1.bottom")])],"isStart":false});
            fillet(context, id + "F15", {"entities" : qUnion([Q0]), "radius" : 2 * mm, "tangentPropagation" : true, "allowEdgeOverflow" : false});
        }
        {
            var Q0;
            {var subQ0=sQuery(id+"F0.wireOp",EDGE,"E21.filletArc");var subQ1=sQuery(id+"F0.wireOp",EDGE,"E7");var subQ2=sQuery(id+"F0.wireOp",EDGE,"E6");var subQ3=sQuery(id+"F0.wireOp",EDGE,"E5");var subQ4=sQuery(id+"F0.wireOp",EDGE,"E4");var subQ5=sQuery(id+"F0.wireOp",EDGE,"E22.filletArc");var subQ6=sQuery(id+"F0.wireOp",EDGE,"E1.bottom");var subQ7=sQuery(id+"F0.wireOp",EDGE,"E1.right");var subQ8=sQuery(id+"F0.wireOp",EDGE,"E1.top");var subQ9=sQuery(id+"F0.wireOp",EDGE,"E1.left");var subQ10=sQuery(id+"F0.wireOp",EDGE,"E23.filletArc");var subQ11=sQuery(id+"F0.wireOp",EDGE,"E24.filletArc");Q0=makeQuery(id+"F2.boolean.opBoolean","SPLIT",FACE,{"disambiguationData":[TD([makeQuery(id+"F1.opExtrude","SWEPT_FACE",FACE,{"disambiguationData":[OSD([subQ6])]})])],"derivedFrom":makeQuery(id+"F1.opExtrude","CAP_FACE",FACE,{"disambiguationData":[OSD([subQ6,subQ8,subQ9,subQ7,subQ4,subQ3,subQ2,subQ1,subQ0,subQ5,subQ10,subQ11])],"isStart":true})});}
            var sketch = newSketch(context, id + "F16", { "sketchPlane" : qUnion([Q0])});
            skLineSegment(sketch, "E79", {"start": v(0, 74.25) * mm, "end": v(0, 104.25) * mm, "construction": true});
            skCircle(sketch, "E80", {"center": v(0, 104.25) * mm, "radius": 6 * mm});
            skArc(sketch, "E81", {"start": v(15, 104.25) * mm, "mid": v(0, 119.25) * mm, "end": v(-15, 104.25) * mm});
            skLineSegment(sketch, "E82", {"start": v(-15, 104.25) * mm, "end": v(-15, 92.25) * mm});
            skLineSegment(sketch, "E83", {"start": v(15, 104.25) * mm, "end": v(15, 92.25) * mm});
            skLineSegment(sketch, "E84", {"start": v(15, 92.25) * mm, "end": v(33, 74.25) * mm});
            skLineSegment(sketch, "E85", {"start": v(-15, 92.25) * mm, "end": v(-33, 74.25) * mm});
            skLineSegment(sketch, "E86", {"start": v(-74.25, 0) * mm, "end": v(74.25, 0) * mm, "construction": true});
            skLineSegment(sketch, "E87.MirrorCS", {"start": v(-15, -104.25) * mm, "end": v(-15, -92.25) * mm});
            skLineSegment(sketch, "E88.MirrorCS", {"start": v(15, -104.25) * mm, "end": v(15, -92.25) * mm});
            skLineSegment(sketch, "E89.MirrorCS", {"start": v(15, -92.25) * mm, "end": v(33, -74.25) * mm});
            skLineSegment(sketch, "E90.MirrorCS", {"start": v(-15, -92.25) * mm, "end": v(-33, -74.25) * mm});
            skLineSegment(sketch, "E91.MirrorCS", {"start": v(0, -74.25) * mm, "end": v(0, -104.25) * mm, "construction": true});
            skCircle(sketch, "E92.MirrorC", {"center": v(0, -104.25) * mm, "radius": 6 * mm});
            skArc(sketch, "E93.MirrorCS", {"start": v(15, -104.25) * mm, "mid": v(0, -119.25) * mm, "end": v(-15, -104.25) * mm});
            skSolve(sketch);
        }
        {
            var Q0;
            Q0=makeQuery(id+"F16.imprint","IMPRINT",FACE,{"disambiguationData":[TD([[makeQuery(id+"F16.imprint","IMPRINT",EDGE,{"derivedFrom":sQuery(id+"F16.wireOp",EDGE,"E80")}),-1.0]])]});
            var Q1;
            Q1=makeQuery(id+"F16.imprint","IMPRINT",FACE,{"disambiguationData":[TD([[makeQuery(id+"F16.imprint","IMPRINT",EDGE,{"derivedFrom":makeQuery(id+"F1.opExtrude","CAP_EDGE",EDGE,{"disambiguationData":[OSD([sQuery(id+"F0.wireOp",EDGE,"E1.left")])],"isStart":true})}),-1.0]])]});
            var Q2;
            Q2=makeQuery(id+"F16.imprint","IMPRINT",FACE,{"disambiguationData":[TD([[makeQuery(id+"F16.imprint","IMPRINT",EDGE,{"derivedFrom":sQuery(id+"F16.wireOp",EDGE,"E87.MirrorCS")}),-1.0]])]});
            extrude(context, id + "F17", {"entities" : qUnion([Q0, Q1, Q2]), "operationType" : NewBodyOperationType.ADD, "depth" : 25 * mm});
        }
    });
